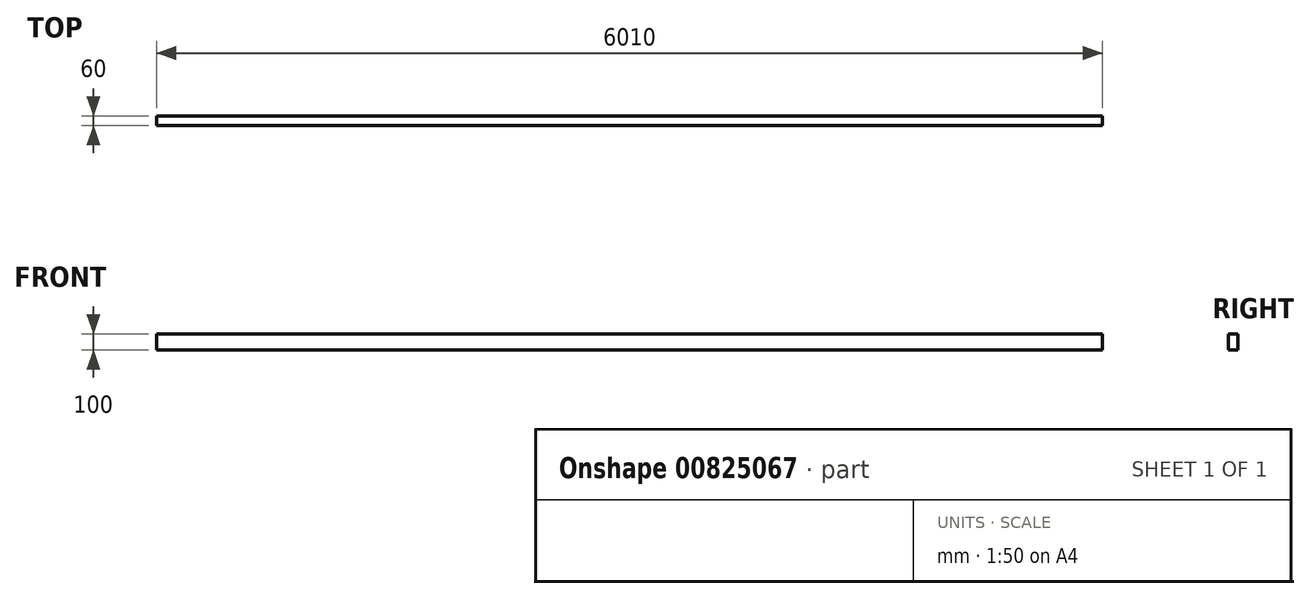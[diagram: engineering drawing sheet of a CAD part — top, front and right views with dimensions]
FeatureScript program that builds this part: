
annotation { "Feature Type Name" : "Feature", "Feature Type Description" : "" }
export const myFeature = defineFeature(function(context is Context, id is Id, definition is map)
    precondition{}
    {
        {
            var Q0;
            Q0=qCreatedBy(makeId("Top.planeOp"),FACE);
            var sketch = newSketch(context, id + "F0", { "sketchPlane" : qUnion([Q0])});
            skLineSegment(sketch, "E0.bottom", {"start": v(-508.95, 44.94) * mm, "end": v(5501.05, 44.94) * mm});
            skLineSegment(sketch, "E0.top", {"start": v(-508.95, -15.06) * mm, "end": v(5501.05, -15.06) * mm});
            skLineSegment(sketch, "E0.left", {"start": v(-508.95, 44.94) * mm, "end": v(-508.95, -15.06) * mm});
            skLineSegment(sketch, "E0.right", {"start": v(5501.05, 44.94) * mm, "end": v(5501.05, -15.06) * mm});
            skSolve(sketch);
        }
        {
            var Q0;
            Q0 = qSketchRegion(id + "F0", true);
            extrude(context, id + "F1", {"entities" : qUnion([Q0]), "depth" : 100 * mm, "offsetDistance" : 25 * mm});
        }
    });
